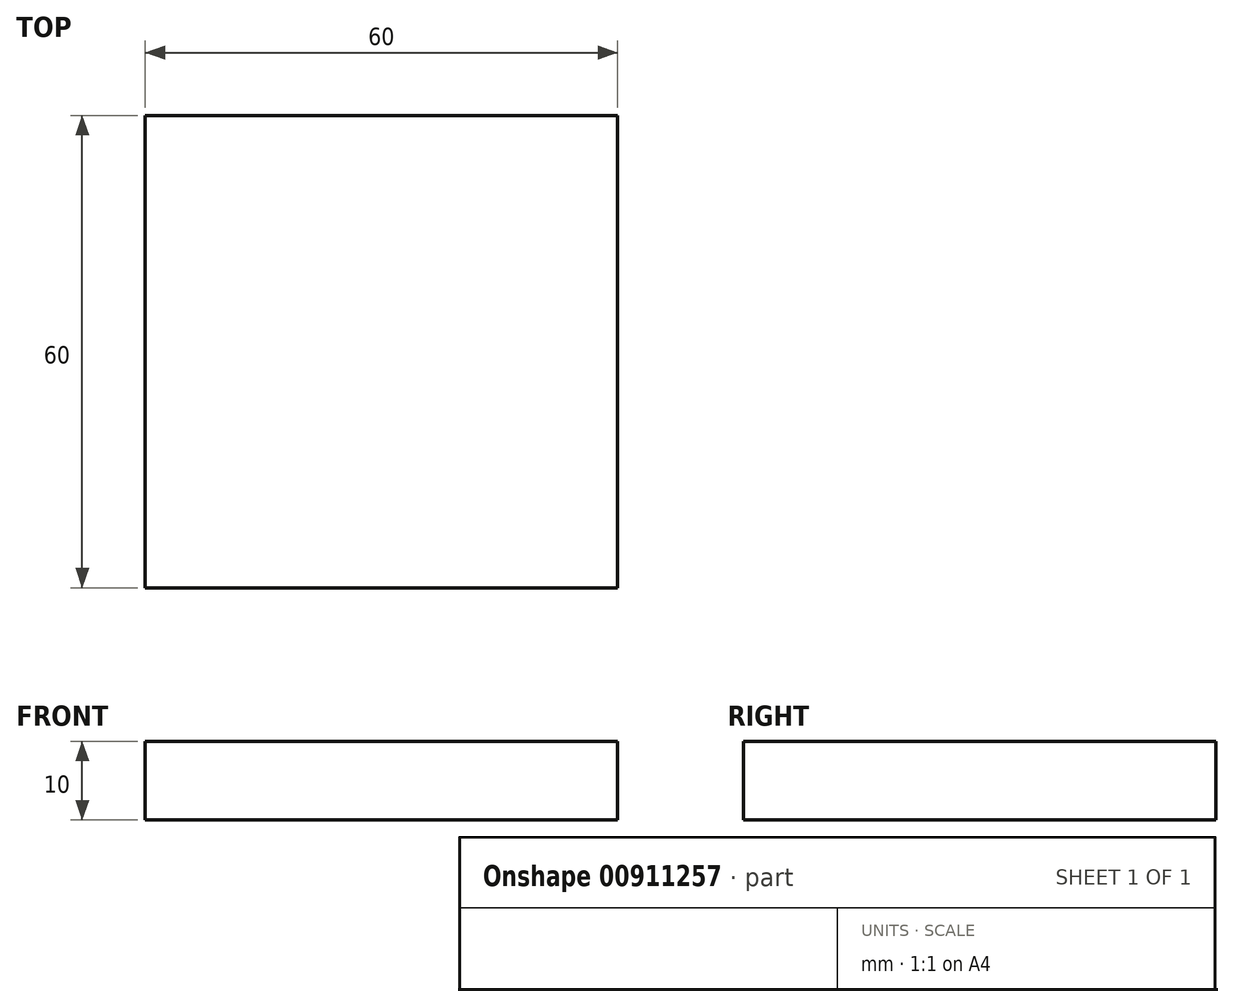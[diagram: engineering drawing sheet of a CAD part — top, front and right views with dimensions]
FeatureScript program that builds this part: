
annotation { "Feature Type Name" : "Feature", "Feature Type Description" : "" }
export const myFeature = defineFeature(function(context is Context, id is Id, definition is map)
    precondition{}
    {
        {
            var Q0;
            Q0=qCreatedBy(makeId("Top.planeOp"),FACE);
            var sketch = newSketch(context, id + "F0", { "sketchPlane" : qUnion([Q0])});
            skLineSegment(sketch, "E0.bottom", {"start": v(30, 30) * mm, "end": v(-30, 30) * mm});
            skLineSegment(sketch, "E0.top", {"start": v(30, -30) * mm, "end": v(-30, -30) * mm});
            skLineSegment(sketch, "E0.left", {"start": v(30, 30) * mm, "end": v(30, -30) * mm});
            skLineSegment(sketch, "E0.right", {"start": v(-30, 30) * mm, "end": v(-30, -30) * mm});
            skPoint(sketch, "E0.middle", {"position": v(0, 0) * mm});
            skSolve(sketch);
        }
        {
            var Q0;
            Q0=makeQuery(id+"F0.imprint","IMPRINT",FACE,{"disambiguationData":[TD([[makeQuery(id+"F0.imprint","IMPRINT",EDGE,{"derivedFrom":sQuery(id+"F0.wireOp",EDGE,"E0.bottom")}),1.0]])]});
            extrude(context, id + "F1", {"entities" : qUnion([Q0]), "depth" : 10 * mm, "offsetDistance" : 25 * mm});
        }
    });
